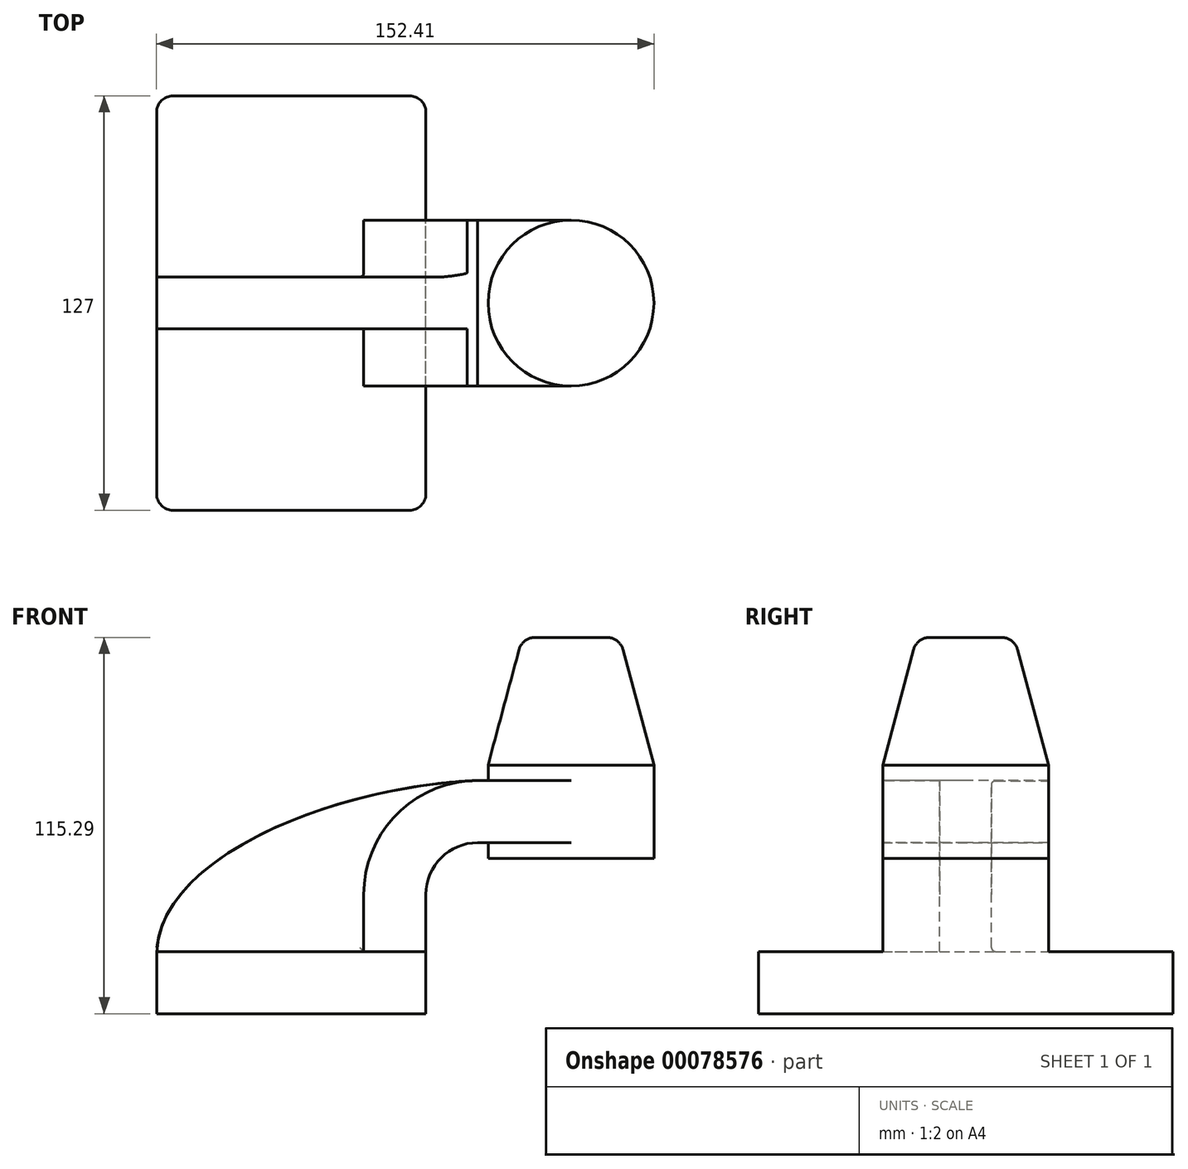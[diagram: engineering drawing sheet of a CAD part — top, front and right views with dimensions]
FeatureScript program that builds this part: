
annotation { "Feature Type Name" : "Feature", "Feature Type Description" : "" }
export const myFeature = defineFeature(function(context is Context, id is Id, definition is map)
    precondition{}
    {
        {
            var Q0;
            Q0=qCreatedBy(makeId("Front.planeOp"),FACE);
            var sketch = newSketch(context, id + "F0", { "sketchPlane" : qUnion([Q0])});
            skLineSegment(sketch, "E0.rect.bottom", {"start": v(-41.28, 9.52) * mm, "end": v(41.28, 9.52) * mm});
            skLineSegment(sketch, "E0.rect.top", {"start": v(-41.28, -9.52) * mm, "end": v(41.28, -9.52) * mm});
            skLineSegment(sketch, "E0.rect.left", {"start": v(-41.28, 9.52) * mm, "end": v(-41.28, -9.52) * mm});
            skLineSegment(sketch, "E0.rect.right", {"start": v(41.28, 9.52) * mm, "end": v(41.28, -9.52) * mm});
            skPoint(sketch, "E0.rect.middle", {"position": v(0, 0) * mm});
            skLineSegment(sketch, "E1", {"start": v(41.28, 9.52) * mm, "end": v(41.28, 27) * mm});
            skArc(sketch, "E2", {"start": v(41.28, 27) * mm, "mid": v(45.92, 38.23) * mm, "end": v(57.15, 42.88) * mm});
            skLineSegment(sketch, "E3", {"start": v(57.15, 42.88) * mm, "end": v(85.72, 42.88) * mm});
            skLineSegment(sketch, "E4.rect.bottom", {"start": v(60.32, 38.1) * mm, "end": v(111.12, 38.1) * mm});
            skLineSegment(sketch, "E4.rect.top", {"start": v(60.32, 66.68) * mm, "end": v(111.12, 66.68) * mm});
            skLineSegment(sketch, "E4.rect.left", {"start": v(60.32, 38.1) * mm, "end": v(60.32, 66.68) * mm});
            skLineSegment(sketch, "E4.rect.right", {"start": v(111.13, 38.1) * mm, "end": v(111.12, 66.68) * mm});
            skPoint(sketch, "E4.rect.middle", {"position": v(85.72, 52.39) * mm});
            skLineSegment(sketch, "E5.0", {"start": v(57.15, 61.93) * mm, "end": v(85.72, 61.93) * mm});
            skArc(sketch, "E5.1", {"start": v(22.23, 27) * mm, "mid": v(32.45, 51.7) * mm, "end": v(57.15, 61.93) * mm});
            skLineSegment(sketch, "E5.2", {"start": v(22.23, 9.52) * mm, "end": v(22.23, 27) * mm});
            skLineSegment(sketch, "E6", {"start": v(85.72, 38.1) * mm, "end": v(85.72, 66.68) * mm});
            skFitSpline(sketch, "E7", {"points": [v(-41.28, 9.53) * mm, v(57.15, 61.93) * mm], "startDerivative": vector(5.2, 92.34) * mm, "endDerivative": vector(120.92, 4.22) * mm});
            skSolve(sketch);
        }
        {
            var Q0;
            Q0=makeQuery(id+"F0.imprint","IMPRINT",FACE,{"disambiguationData":[TD([[makeQuery(id+"F0.imprint","IMPRINT",EDGE,{"derivedFrom":sQuery(id+"F0.wireOp",EDGE,"E0.rect.top")}),1.0]])]});
            extrude(context, id + "F1", {"entities" : qUnion([Q0]), "endBound" : BoundingType.SYMMETRIC, "depth" : 127 * mm});
        }
        {
            var Q0;
            {var subQ9=sQuery(id+"F0.wireOp",EDGE,"E1");Q0=makeQuery(id+"F0.imprint","IMPRINT",FACE,{"disambiguationData":[TD([[makeQuery(id+"F0.imprint","IMPRINT",EDGE,{"derivedFrom":subQ9}),1.0]])]});}
            var Q1;
            {var subQ0=sQuery(id+"F0.wireOp",EDGE,"E6");var subQ1=sQuery(id+"F0.wireOp",EDGE,"E3");var subQ2=makeQuery(id+"F0.imprint","INTERSECT",VERTEX,{"derivedFrom":[subQ1,subQ0]});Q1=makeQuery(id+"F0.imprint","IMPRINT",FACE,{"disambiguationData":[TD([[makeQuery(id+"F0.imprint","IMPRINT",EDGE,{"disambiguationData":[TD([[subQ2,1.0]])],"derivedFrom":subQ1}),1.0]])]});}
            extrude(context, id + "F2", {"entities" : qUnion([Q0, Q1]), "operationType" : NewBodyOperationType.ADD, "endBound" : BoundingType.SYMMETRIC, "depth" : 50.8 * mm});
        }
        {
            var Q0;
            {var subQ3=sQuery(id+"F0.wireOp",EDGE,"E5.2");Q0=makeQuery(id+"F0.imprint","IMPRINT",FACE,{"disambiguationData":[TD([[makeQuery(id+"F0.imprint","IMPRINT",EDGE,{"derivedFrom":subQ3}),1.0]])]});}
            extrude(context, id + "F3", {"entities" : qUnion([Q0]), "operationType" : NewBodyOperationType.ADD, "endBound" : BoundingType.SYMMETRIC, "depth" : 15.88 * mm});
        }
        {
            var Q0;
            {var subQ5=sQuery(id+"F0.wireOp",EDGE,"E4.rect.right");Q0=makeQuery(id+"F0.imprint","IMPRINT",FACE,{"disambiguationData":[TD([[makeQuery(id+"F0.imprint","IMPRINT",EDGE,{"derivedFrom":subQ5}),1.0]])]});}
            var Q1;
            Q1=sQuery(id+"F0.wireOp",EDGE,"E6");
            revolve(context, id + "F4", {"operationType" : NewBodyOperationType.ADD, "entities" : qUnion([Q0]), "axis" : qUnion([Q1]), "revolveType" : RevolveType.FULL});
        }
        {
            var Q0;
            Q0=makeQuery(id+"F1.opExtrude","CAP_EDGE",EDGE,{"disambiguationData":[OSD([sQuery(id+"F0.wireOp",EDGE,"E0.rect.right")])],"isStart":false});
            var Q1;
            Q1=makeQuery(id+"F1.opExtrude","CAP_EDGE",EDGE,{"disambiguationData":[OSD([sQuery(id+"F0.wireOp",EDGE,"E0.rect.left")])],"isStart":false});
            var Q2;
            Q2=makeQuery(id+"F1.opExtrude","CAP_EDGE",EDGE,{"disambiguationData":[OSD([sQuery(id+"F0.wireOp",EDGE,"E0.rect.right")])],"isStart":true});
            var Q3;
            Q3=makeQuery(id+"F1.opExtrude","CAP_EDGE",EDGE,{"disambiguationData":[OSD([sQuery(id+"F0.wireOp",EDGE,"E0.rect.left")])],"isStart":true});
            fillet(context, id + "F5", {"entities" : qUnion([Q0, Q1, Q2, Q3]), "radius" : 5.08 * mm, "tangentPropagation" : true, "allowEdgeOverflow" : false});
        }
        {
            var Q0;
            Q0=makeQuery(id+"F4.opRevolve","SWEPT_FACE",FACE,{"disambiguationData":[OSD([sQuery(id+"F0.wireOp",EDGE,"E4.rect.top")])]});
            extrude(context, id + "F6", {"entities" : qUnion([Q0]), "operationType" : NewBodyOperationType.ADD, "depth" : 39.08 * mm, "hasDraft" : true, "draftAngle" : 15 * degree, "draftPullDirection" : true});
        }
        {
            var Q0;
            Q0=makeQuery(id+"F3.opExtrude","CAP_EDGE",EDGE,{"disambiguationData":[OSD([sQuery(id+"F0.wireOp",EDGE,"E5.1")])],"isStart":false});
            var Q1;
            Q1=makeQuery(id+"F3.opExtrude","CAP_EDGE",EDGE,{"disambiguationData":[OSD([sQuery(id+"F0.wireOp",EDGE,"E5.2")])],"isStart":false});
            var Q2;
            Q2=makeQuery(id+"F3.opExtrude","CAP_EDGE",EDGE,{"disambiguationData":[OSD([sQuery(id+"F0.wireOp",EDGE,"E0.rect.bottom")])],"isStart":false});
            var Q3;
            {var subQ0=sQuery(id+"F0.wireOp",EDGE,"E0.rect.bottom");var subQ1=sQuery(id+"F0.wireOp",EDGE,"E7");var subQ2=sQuery(id+"F0.wireOp",EDGE,"E5.2");var subQ3=sQuery(id+"F0.wireOp",EDGE,"E5.1");Q3=makeQuery(id+"F3.boolean.opBoolean","SPLIT",EDGE,{"disambiguationData":[TD([makeQuery(id+"F3.opExtrude","CAP_FACE",FACE,{"disambiguationData":[OSD([subQ0,subQ3,subQ2,subQ1])],"isStart":false})])],"derivedFrom":makeQuery(id+"F2.opExtrude","SWEPT_EDGE",EDGE,{"disambiguationData":[OSD([subQ0,subQ2])]})});}
            var Q4;
            Q4=makeQuery(id+"F2.opExtrude","CAP_EDGE",EDGE,{"disambiguationData":[OSD([sQuery(id+"F0.wireOp",EDGE,"E0.rect.bottom")])],"isStart":false});
            var Q5;
            Q5=makeQuery(id+"F3.opExtrude","CAP_EDGE",EDGE,{"disambiguationData":[OSD([sQuery(id+"F0.wireOp",EDGE,"E5.1")])],"isStart":true});
            var Q6;
            Q6=makeQuery(id+"F3.opExtrude","CAP_EDGE",EDGE,{"disambiguationData":[OSD([sQuery(id+"F0.wireOp",EDGE,"E5.2")])],"isStart":true});
            var Q7;
            Q7=makeQuery(id+"F3.opExtrude","CAP_EDGE",EDGE,{"disambiguationData":[OSD([sQuery(id+"F0.wireOp",EDGE,"E0.rect.bottom")])],"isStart":true});
            var Q8;
            {var subQ0=sQuery(id+"F0.wireOp",EDGE,"E0.rect.bottom");var subQ1=sQuery(id+"F0.wireOp",EDGE,"E7");var subQ2=sQuery(id+"F0.wireOp",EDGE,"E5.2");var subQ3=sQuery(id+"F0.wireOp",EDGE,"E5.1");Q8=makeQuery(id+"F3.boolean.opBoolean","SPLIT",EDGE,{"disambiguationData":[TD([makeQuery(id+"F3.opExtrude","CAP_FACE",FACE,{"disambiguationData":[OSD([subQ0,subQ3,subQ2,subQ1])],"isStart":true})])],"derivedFrom":makeQuery(id+"F2.opExtrude","SWEPT_EDGE",EDGE,{"disambiguationData":[OSD([subQ0,subQ2])]})});}
            var Q9;
            Q9=makeQuery(id+"F2.opExtrude","CAP_EDGE",EDGE,{"disambiguationData":[OSD([sQuery(id+"F0.wireOp",EDGE,"E0.rect.bottom")])],"isStart":true});
            fillet(context, id + "F7", {"entities" : qUnion([Q0, Q1, Q2, Q3, Q4, Q5, Q6, Q7, Q8, Q9]), "radius" : 1.27 * mm, "tangentPropagation" : true, "allowEdgeOverflow" : false});
        }
        {
            var Q0;
            Q0=makeQuery(id+"F6.opExtrude","CAP_EDGE",EDGE,{"disambiguationData":[OSD([sQuery(id+"F0.wireOp",EDGE,"E4.rect.top"),sQuery(id+"F0.wireOp",EDGE,"E4.rect.right")])],"isStart":false});
            fillet(context, id + "F8", {"entities" : qUnion([Q0]), "radius" : 5.08 * mm, "tangentPropagation" : true, "allowEdgeOverflow" : false});
        }
    });
